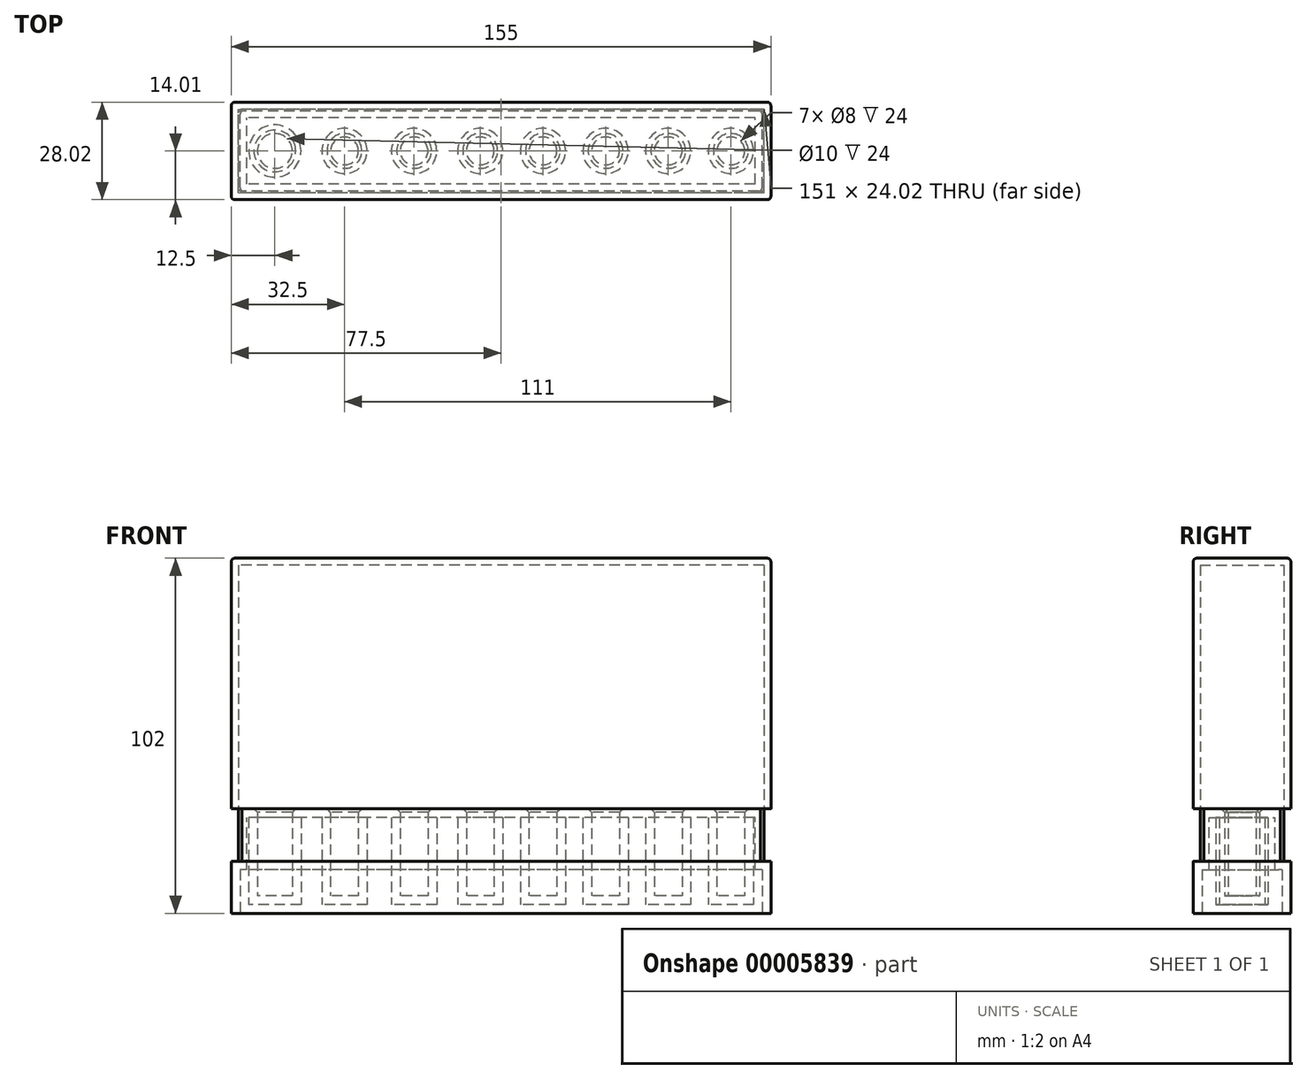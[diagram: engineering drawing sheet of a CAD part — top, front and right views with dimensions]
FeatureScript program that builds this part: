
annotation { "Feature Type Name" : "Feature", "Feature Type Description" : "" }
export const myFeature = defineFeature(function(context is Context, id is Id, definition is map)
    precondition{}
    {
        {
            var Q0;
            Q0=qCreatedBy(makeId("Top.planeOp"),FACE);
            var sketch = newSketch(context, id + "F0", { "sketchPlane" : qUnion([Q0])});
            skCircle(sketch, "E0", {"center": v(-65.5, 0) * mm, "radius": 7.5 * mm, "construction": true});
            skCircle(sketch, "E1.1.0.0", {"center": v(-45.5, 0) * mm, "radius": 7.5 * mm, "construction": true});
            skCircle(sketch, "E1.2.0.0", {"center": v(-25.5, 0) * mm, "radius": 7.5 * mm, "construction": true});
            skCircle(sketch, "E1.3.0.0", {"center": v(-6.5, 0) * mm, "radius": 6.5 * mm, "construction": true});
            skCircle(sketch, "E1.4.0.0", {"center": v(11.5, 0) * mm, "radius": 6.5 * mm, "construction": true});
            skCircle(sketch, "E1.5.0.0", {"center": v(29.5, 0) * mm, "radius": 6.5 * mm, "construction": true});
            skCircle(sketch, "E1.6.0.0", {"center": v(47.5, 0) * mm, "radius": 6.5 * mm, "construction": true});
            skCircle(sketch, "E1.7.0.0", {"center": v(65.5, 0) * mm, "radius": 6.5 * mm, "construction": true});
            skCircle(sketch, "E2", {"center": v(-65.5, 0) * mm, "radius": 5 * mm});
            skCircle(sketch, "E3", {"center": v(-45.5, 0) * mm, "radius": 4 * mm});
            skCircle(sketch, "E4", {"center": v(-25.5, 0) * mm, "radius": 4 * mm});
            skCircle(sketch, "E5", {"center": v(-6.5, 0) * mm, "radius": 4 * mm});
            skCircle(sketch, "E6", {"center": v(11.5, 0) * mm, "radius": 4 * mm});
            skCircle(sketch, "E7", {"center": v(29.5, 0) * mm, "radius": 4 * mm});
            skCircle(sketch, "E8", {"center": v(47.5, 0) * mm, "radius": 4 * mm});
            skCircle(sketch, "E9", {"center": v(65.5, 0) * mm, "radius": 4 * mm});
            skPoint(sketch, "E10", {"position": v(0, 0) * mm});
            skLineSegment(sketch, "E11.bottom", {"start": v(77, -14) * mm, "end": v(-78, -14) * mm});
            skLineSegment(sketch, "E11.top", {"start": v(77, 14) * mm, "end": v(-78, 14) * mm});
            skLineSegment(sketch, "E11.left", {"start": v(77, -14) * mm, "end": v(77, 14) * mm});
            skLineSegment(sketch, "E11.right", {"start": v(-78, -14) * mm, "end": v(-78, 14) * mm});
            skLineSegment(sketch, "E12", {"start": v(-82.74, 0) * mm, "end": v(89.14, 0) * mm, "construction": true});
            skLineSegment(sketch, "E13.0", {"start": v(-76, -12) * mm, "end": v(-76, 12) * mm});
            skLineSegment(sketch, "E13.1", {"start": v(75, -12) * mm, "end": v(-76, -12) * mm});
            skLineSegment(sketch, "E13.2", {"start": v(75, -12) * mm, "end": v(75, 12) * mm});
            skLineSegment(sketch, "E13.3", {"start": v(75, 12) * mm, "end": v(-76, 12) * mm});
            skSolve(sketch);
        }
        {
            var Q0;
            Q0=makeQuery(id+"F0.imprint","IMPRINT",FACE,{"disambiguationData":[TD([[makeQuery(id+"F0.imprint","IMPRINT",EDGE,{"derivedFrom":sQuery(id+"F0.wireOp",EDGE,"E2")}),-1.0]])]});
            var Q1;
            Q1=makeQuery(id+"F0.imprint","IMPRINT",FACE,{"disambiguationData":[TD([[makeQuery(id+"F0.imprint","IMPRINT",EDGE,{"derivedFrom":sQuery(id+"F0.wireOp",EDGE,"E11.bottom")}),-1.0]])]});
            extrude(context, id + "F1", {"entities" : qUnion([Q0, Q1]), "depth" : 25 * mm, "offsetDistance" : 25 * mm});
        }
        {
            var Q0;
            Q0=makeQuery(id+"F0.imprint","IMPRINT",FACE,{"disambiguationData":[TD([[makeQuery(id+"F0.imprint","IMPRINT",EDGE,{"derivedFrom":sQuery(id+"F0.wireOp",EDGE,"E6")}),1.0]])]});
            var Q1;
            Q1=makeQuery(id+"F0.imprint","IMPRINT",FACE,{"disambiguationData":[TD([[makeQuery(id+"F0.imprint","IMPRINT",EDGE,{"derivedFrom":sQuery(id+"F0.wireOp",EDGE,"E3")}),1.0]])]});
            var Q2;
            Q2=makeQuery(id+"F0.imprint","IMPRINT",FACE,{"disambiguationData":[TD([[makeQuery(id+"F0.imprint","IMPRINT",EDGE,{"derivedFrom":sQuery(id+"F0.wireOp",EDGE,"E2")}),1.0]])]});
            var Q3;
            Q3=makeQuery(id+"F0.imprint","IMPRINT",FACE,{"disambiguationData":[TD([[makeQuery(id+"F0.imprint","IMPRINT",EDGE,{"derivedFrom":sQuery(id+"F0.wireOp",EDGE,"E4")}),1.0]])]});
            var Q4;
            Q4=makeQuery(id+"F0.imprint","IMPRINT",FACE,{"disambiguationData":[TD([[makeQuery(id+"F0.imprint","IMPRINT",EDGE,{"derivedFrom":sQuery(id+"F0.wireOp",EDGE,"E5")}),1.0]])]});
            var Q5;
            Q5=makeQuery(id+"F0.imprint","IMPRINT",FACE,{"disambiguationData":[TD([[makeQuery(id+"F0.imprint","IMPRINT",EDGE,{"derivedFrom":sQuery(id+"F0.wireOp",EDGE,"E7")}),1.0]])]});
            var Q6;
            Q6=makeQuery(id+"F0.imprint","IMPRINT",FACE,{"disambiguationData":[TD([[makeQuery(id+"F0.imprint","IMPRINT",EDGE,{"derivedFrom":sQuery(id+"F0.wireOp",EDGE,"E8")}),1.0]])]});
            var Q7;
            Q7=makeQuery(id+"F0.imprint","IMPRINT",FACE,{"disambiguationData":[TD([[makeQuery(id+"F0.imprint","IMPRINT",EDGE,{"derivedFrom":sQuery(id+"F0.wireOp",EDGE,"E2")}),-1.0]])]});
            var Q8;
            Q8=makeQuery(id+"F0.imprint","IMPRINT",FACE,{"disambiguationData":[TD([[makeQuery(id+"F0.imprint","IMPRINT",EDGE,{"derivedFrom":sQuery(id+"F0.wireOp",EDGE,"E9")}),1.0]])]});
            var Q9;
            Q9=makeQuery(id+"F0.imprint","IMPRINT",FACE,{"disambiguationData":[TD([[makeQuery(id+"F0.imprint","IMPRINT",EDGE,{"derivedFrom":sQuery(id+"F0.wireOp",EDGE,"E11.bottom")}),-1.0]])]});
            extrude(context, id + "F2", {"entities" : qUnion([Q0, Q1, Q2, Q3, Q4, Q5, Q6, Q7, Q8, Q9]), "operationType" : NewBodyOperationType.ADD, "oppositeDirection" : true, "depth" : 5 * mm, "offsetDistance" : 25 * mm});
        }
        {
            var Q0;
            Q0=makeQuery(id+"F1.opExtrude","CAP_FACE",FACE,{"disambiguationData":[OSD([sQuery(id+"F0.wireOp",EDGE,"E2"),sQuery(id+"F0.wireOp",EDGE,"E3"),sQuery(id+"F0.wireOp",EDGE,"E4"),sQuery(id+"F0.wireOp",EDGE,"E5"),sQuery(id+"F0.wireOp",EDGE,"E6"),sQuery(id+"F0.wireOp",EDGE,"E7"),sQuery(id+"F0.wireOp",EDGE,"E8"),sQuery(id+"F0.wireOp",EDGE,"E9"),sQuery(id+"F0.wireOp",EDGE,"E11.bottom"),sQuery(id+"F0.wireOp",EDGE,"E11.top"),sQuery(id+"F0.wireOp",EDGE,"E11.left"),sQuery(id+"F0.wireOp",EDGE,"E11.right")])],"isStart":false});
            var sketch = newSketch(context, id + "F3", { "sketchPlane" : qUnion([Q0])});
            skLineSegment(sketch, "E14.0", {"start": v(75, -12) * mm, "end": v(-76, -12) * mm});
            skLineSegment(sketch, "E15.0", {"start": v(-76, -12) * mm, "end": v(-76, 12) * mm});
            skLineSegment(sketch, "E16.0", {"start": v(75, 12) * mm, "end": v(-76, 12) * mm});
            skLineSegment(sketch, "E17.0", {"start": v(77, -14) * mm, "end": v(77, 14) * mm});
            skLineSegment(sketch, "E18.0", {"start": v(75, -12) * mm, "end": v(75, 12) * mm});
            skSolve(sketch);
        }
        {
            var Q0;
            Q0=makeQuery(id+"F3.imprint","IMPRINT",FACE,{"disambiguationData":[TD([[makeQuery(id+"F3.imprint","IMPRINT",EDGE,{"derivedFrom":sQuery(id+"F3.wireOp",EDGE,"E14.0")}),1.0]])]});
            var Q1;
            Q1=makeQuery(id+"F3.imprint","IMPRINT",FACE,{"disambiguationData":[TD([[makeQuery(id+"F3.imprint","IMPRINT",EDGE,{"derivedFrom":sQuery(id+"F3.wireOp",EDGE,"E14.0")}),-1.0]])]});
            var Q2;
            Q2=makeQuery(id+"F3.imprint","IMPRINT",FACE,{"disambiguationData":[TD([[makeQuery(id+"F3.imprint","IMPRINT",EDGE,{"derivedFrom":makeQuery(id+"F1.opExtrude","CAP_EDGE",EDGE,{"disambiguationData":[OSD([sQuery(id+"F0.wireOp",EDGE,"E2")])],"isStart":false})}),1.0]])]});
            var Q3;
            Q3=makeQuery(id+"F3.imprint","IMPRINT",FACE,{"disambiguationData":[TD([[makeQuery(id+"F3.imprint","IMPRINT",EDGE,{"derivedFrom":makeQuery(id+"F1.opExtrude","CAP_EDGE",EDGE,{"disambiguationData":[OSD([sQuery(id+"F0.wireOp",EDGE,"E3")])],"isStart":false})}),1.0]])]});
            var Q4;
            Q4=makeQuery(id+"F3.imprint","IMPRINT",FACE,{"disambiguationData":[TD([[makeQuery(id+"F3.imprint","IMPRINT",EDGE,{"derivedFrom":makeQuery(id+"F1.opExtrude","CAP_EDGE",EDGE,{"disambiguationData":[OSD([sQuery(id+"F0.wireOp",EDGE,"E4")])],"isStart":false})}),1.0]])]});
            var Q5;
            Q5=makeQuery(id+"F3.imprint","IMPRINT",FACE,{"disambiguationData":[TD([[makeQuery(id+"F3.imprint","IMPRINT",EDGE,{"derivedFrom":makeQuery(id+"F1.opExtrude","CAP_EDGE",EDGE,{"disambiguationData":[OSD([sQuery(id+"F0.wireOp",EDGE,"E5")])],"isStart":false})}),1.0]])]});
            var Q6;
            Q6=makeQuery(id+"F3.imprint","IMPRINT",FACE,{"disambiguationData":[TD([[makeQuery(id+"F3.imprint","IMPRINT",EDGE,{"derivedFrom":makeQuery(id+"F1.opExtrude","CAP_EDGE",EDGE,{"disambiguationData":[OSD([sQuery(id+"F0.wireOp",EDGE,"E6")])],"isStart":false})}),1.0]])]});
            var Q7;
            Q7=makeQuery(id+"F3.imprint","IMPRINT",FACE,{"disambiguationData":[TD([[makeQuery(id+"F3.imprint","IMPRINT",EDGE,{"derivedFrom":makeQuery(id+"F1.opExtrude","CAP_EDGE",EDGE,{"disambiguationData":[OSD([sQuery(id+"F0.wireOp",EDGE,"E7")])],"isStart":false})}),1.0]])]});
            var Q8;
            Q8=makeQuery(id+"F3.imprint","IMPRINT",FACE,{"disambiguationData":[TD([[makeQuery(id+"F3.imprint","IMPRINT",EDGE,{"derivedFrom":makeQuery(id+"F1.opExtrude","CAP_EDGE",EDGE,{"disambiguationData":[OSD([sQuery(id+"F0.wireOp",EDGE,"E8")])],"isStart":false})}),1.0]])]});
            var Q9;
            Q9=makeQuery(id+"F3.imprint","IMPRINT",FACE,{"disambiguationData":[TD([[makeQuery(id+"F3.imprint","IMPRINT",EDGE,{"derivedFrom":makeQuery(id+"F1.opExtrude","CAP_EDGE",EDGE,{"disambiguationData":[OSD([sQuery(id+"F0.wireOp",EDGE,"E9")])],"isStart":false})}),1.0]])]});
            extrude(context, id + "F4", {"entities" : qUnion([Q0, Q1, Q2, Q3, Q4, Q5, Q6, Q7, Q8, Q9]), "depth" : 72 * mm, "offsetDistance" : 25 * mm, "hasSecondDirection" : true, "secondDirectionOppositeDirection" : true, "secondDirectionDepth" : 15 * mm});
        }
        {
            var Q0;
            Q0=makeQuery(id+"F4.opExtrude","CAP_FACE",FACE,{"disambiguationData":[OSD([sQuery(id+"F0.wireOp",EDGE,"E11.bottom"),sQuery(id+"F0.wireOp",EDGE,"E11.top"),sQuery(id+"F0.wireOp",EDGE,"E11.right"),sQuery(id+"F3.wireOp",EDGE,"E17.0")])],"isStart":true});
            shell(context, id + "F5", {"entities" : qUnion([Q0]), "thickness" : 2 * mm});
        }
        {
            var Q0;
            Q0=makeQuery(id+"F3.imprint","IMPRINT",FACE,{"disambiguationData":[TD([[makeQuery(id+"F3.imprint","IMPRINT",EDGE,{"derivedFrom":sQuery(id+"F3.wireOp",EDGE,"E14.0")}),1.0]])]});
            extrude(context, id + "F6", {"entities" : qUnion([Q0]), "operationType" : NewBodyOperationType.REMOVE, "oppositeDirection" : true, "depth" : 15 * mm, "offsetDistance" : 25 * mm});
        }
        {
            var Q0;
            Q0=makeQuery(id+"F2.opExtrude","CAP_FACE",FACE,{"disambiguationData":[OSD([sQuery(id+"F0.wireOp",EDGE,"E11.bottom"),sQuery(id+"F0.wireOp",EDGE,"E11.top"),sQuery(id+"F0.wireOp",EDGE,"E11.left"),sQuery(id+"F0.wireOp",EDGE,"E11.right")])],"isStart":false});
            shell(context, id + "F7", {"entities" : qUnion([Q0]), "thickness" : 2.5 * mm});
        }
        {
            var Q0;
            Q0=makeQuery(id+"F6.boolean.opBoolean","COPY",EDGE,{"derivedFrom":makeQuery(id+"F6.opExtrude","CAP_EDGE",EDGE,{"disambiguationData":[OSD([sQuery(id+"F3.wireOp",EDGE,"E16.0")])],"isStart":true})});
            var Q1;
            Q1=makeQuery(id+"F6.boolean.opBoolean","COPY",EDGE,{"derivedFrom":makeQuery(id+"F6.opExtrude","CAP_EDGE",EDGE,{"disambiguationData":[OSD([sQuery(id+"F3.wireOp",EDGE,"E18.0")])],"isStart":true})});
            var Q2;
            Q2=makeQuery(id+"F6.boolean.opBoolean","COPY",EDGE,{"derivedFrom":makeQuery(id+"F6.opExtrude","CAP_EDGE",EDGE,{"disambiguationData":[OSD([sQuery(id+"F3.wireOp",EDGE,"E14.0")])],"isStart":true})});
            var Q3;
            Q3=makeQuery(id+"F6.boolean.opBoolean","COPY",EDGE,{"derivedFrom":makeQuery(id+"F6.opExtrude","CAP_EDGE",EDGE,{"disambiguationData":[OSD([sQuery(id+"F3.wireOp",EDGE,"E15.0")])],"isStart":true})});
            var Q4;
            Q4=makeQuery(id+"F6.boolean.opBoolean","COPY",EDGE,{"derivedFrom":makeQuery(id+"F6.opExtrude","SWEPT_EDGE",EDGE,{"disambiguationData":[OSD([sQuery(id+"F3.wireOp",EDGE,"E15.0"),sQuery(id+"F3.wireOp",EDGE,"E16.0")])]})});
            var Q5;
            Q5=makeQuery(id+"F6.boolean.opBoolean","COPY",EDGE,{"derivedFrom":makeQuery(id+"F6.opExtrude","SWEPT_EDGE",EDGE,{"disambiguationData":[OSD([sQuery(id+"F3.wireOp",EDGE,"E16.0"),sQuery(id+"F3.wireOp",EDGE,"E18.0")])]})});
            var Q6;
            Q6=makeQuery(id+"F6.boolean.opBoolean","COPY",EDGE,{"derivedFrom":makeQuery(id+"F6.opExtrude","SWEPT_EDGE",EDGE,{"disambiguationData":[OSD([sQuery(id+"F3.wireOp",EDGE,"E14.0"),sQuery(id+"F3.wireOp",EDGE,"E18.0")])]})});
            var Q7;
            Q7=makeQuery(id+"F6.boolean.opBoolean","COPY",EDGE,{"derivedFrom":makeQuery(id+"F6.opExtrude","SWEPT_EDGE",EDGE,{"disambiguationData":[OSD([sQuery(id+"F3.wireOp",EDGE,"E14.0"),sQuery(id+"F3.wireOp",EDGE,"E15.0")])]})});
            var Q8;
            Q8=makeQuery(id+"F1.opExtrude","CAP_EDGE",EDGE,{"disambiguationData":[OSD([sQuery(id+"F0.wireOp",EDGE,"E2")])],"isStart":false});
            var Q9;
            Q9=makeQuery(id+"F1.opExtrude","CAP_EDGE",EDGE,{"disambiguationData":[OSD([sQuery(id+"F0.wireOp",EDGE,"E3")])],"isStart":false});
            var Q10;
            Q10=makeQuery(id+"F1.opExtrude","CAP_EDGE",EDGE,{"disambiguationData":[OSD([sQuery(id+"F0.wireOp",EDGE,"E4")])],"isStart":false});
            var Q11;
            Q11=makeQuery(id+"F1.opExtrude","CAP_EDGE",EDGE,{"disambiguationData":[OSD([sQuery(id+"F0.wireOp",EDGE,"E5")])],"isStart":false});
            var Q12;
            Q12=makeQuery(id+"F1.opExtrude","CAP_EDGE",EDGE,{"disambiguationData":[OSD([sQuery(id+"F0.wireOp",EDGE,"E6")])],"isStart":false});
            var Q13;
            Q13=makeQuery(id+"F1.opExtrude","CAP_EDGE",EDGE,{"disambiguationData":[OSD([sQuery(id+"F0.wireOp",EDGE,"E7")])],"isStart":false});
            var Q14;
            Q14=makeQuery(id+"F1.opExtrude","CAP_EDGE",EDGE,{"disambiguationData":[OSD([sQuery(id+"F0.wireOp",EDGE,"E8")])],"isStart":false});
            var Q15;
            Q15=makeQuery(id+"F1.opExtrude","CAP_EDGE",EDGE,{"disambiguationData":[OSD([sQuery(id+"F0.wireOp",EDGE,"E9")])],"isStart":false});
            chamfer(context, id + "F8", {"entities" : qUnion([Q0, Q1, Q2, Q3, Q4, Q5, Q6, Q7, Q8, Q9, Q10, Q11, Q12, Q13, Q14, Q15]), "width" : 1 * mm, "tangentPropagation" : true});
        }
        {
            var Q0;
            Q0=makeQuery(id+"F4.opExtrude","SWEPT_EDGE",EDGE,{"disambiguationData":[OSD([sQuery(id+"F0.wireOp",EDGE,"E11.bottom"),sQuery(id+"F3.wireOp",EDGE,"E17.0")])]});
            var Q1;
            Q1=makeQuery(id+"F4.opExtrude","SWEPT_EDGE",EDGE,{"disambiguationData":[OSD([sQuery(id+"F0.wireOp",EDGE,"E11.top"),sQuery(id+"F3.wireOp",EDGE,"E17.0")])]});
            var Q2;
            Q2=makeQuery(id+"F4.opExtrude","SWEPT_EDGE",EDGE,{"disambiguationData":[OSD([sQuery(id+"F0.wireOp",EDGE,"E11.top"),sQuery(id+"F0.wireOp",EDGE,"E11.right")])]});
            var Q3;
            Q3=makeQuery(id+"F4.opExtrude","SWEPT_EDGE",EDGE,{"disambiguationData":[OSD([sQuery(id+"F0.wireOp",EDGE,"E11.bottom"),sQuery(id+"F0.wireOp",EDGE,"E11.right")])]});
            var Q4;
            Q4=makeQuery(id+"F4.opExtrude","CAP_EDGE",EDGE,{"disambiguationData":[OSD([sQuery(id+"F0.wireOp",EDGE,"E11.right")])],"isStart":false});
            var Q5;
            Q5=makeQuery(id+"F4.opExtrude","CAP_EDGE",EDGE,{"disambiguationData":[OSD([sQuery(id+"F0.wireOp",EDGE,"E11.top")])],"isStart":false});
            var Q6;
            Q6=makeQuery(id+"F4.opExtrude","CAP_EDGE",EDGE,{"disambiguationData":[OSD([sQuery(id+"F3.wireOp",EDGE,"E17.0")])],"isStart":false});
            var Q7;
            Q7=makeQuery(id+"F4.opExtrude","CAP_EDGE",EDGE,{"disambiguationData":[OSD([sQuery(id+"F0.wireOp",EDGE,"E11.bottom")])],"isStart":false});
            var Q8;
            {var subQ0=sQuery(id+"F0.wireOp",EDGE,"E11.right");var subQ1=sQuery(id+"F0.wireOp",EDGE,"E11.top");Q8=makeQuery(id+"F2.boolean.opBoolean","MERGE",EDGE,{"derivedFrom":[makeQuery(id+"F1.opExtrude","SWEPT_EDGE",EDGE,{"disambiguationData":[OSD([subQ1,subQ0])]}),makeQuery(id+"F2.opExtrude","SWEPT_EDGE",EDGE,{"disambiguationData":[OSD([subQ1,subQ0])]})]});}
            var Q9;
            {var subQ0=sQuery(id+"F0.wireOp",EDGE,"E11.right");var subQ1=sQuery(id+"F0.wireOp",EDGE,"E11.bottom");Q9=makeQuery(id+"F2.boolean.opBoolean","MERGE",EDGE,{"derivedFrom":[makeQuery(id+"F1.opExtrude","SWEPT_EDGE",EDGE,{"disambiguationData":[OSD([subQ1,subQ0])]}),makeQuery(id+"F2.opExtrude","SWEPT_EDGE",EDGE,{"disambiguationData":[OSD([subQ1,subQ0])]})]});}
            var Q10;
            {var subQ0=sQuery(id+"F0.wireOp",EDGE,"E11.left");var subQ1=sQuery(id+"F0.wireOp",EDGE,"E11.bottom");Q10=makeQuery(id+"F2.boolean.opBoolean","MERGE",EDGE,{"derivedFrom":[makeQuery(id+"F1.opExtrude","SWEPT_EDGE",EDGE,{"disambiguationData":[OSD([subQ1,subQ0])]}),makeQuery(id+"F2.opExtrude","SWEPT_EDGE",EDGE,{"disambiguationData":[OSD([subQ1,subQ0])]})]});}
            var Q11;
            {var subQ0=sQuery(id+"F0.wireOp",EDGE,"E11.left");var subQ1=sQuery(id+"F0.wireOp",EDGE,"E11.top");Q11=makeQuery(id+"F2.boolean.opBoolean","MERGE",EDGE,{"derivedFrom":[makeQuery(id+"F1.opExtrude","SWEPT_EDGE",EDGE,{"disambiguationData":[OSD([subQ1,subQ0])]}),makeQuery(id+"F2.opExtrude","SWEPT_EDGE",EDGE,{"disambiguationData":[OSD([subQ1,subQ0])]})]});}
            var Q12;
            Q12=makeQuery(id+"F7.opShell","OFFSET_EDGE",EDGE,{"disambiguationData":[OSD([sQuery(id+"F0.wireOp",EDGE,"E11.bottom"),sQuery(id+"F0.wireOp",EDGE,"E11.left")])]});
            var Q13;
            Q13=makeQuery(id+"F7.opShell","OFFSET_EDGE",EDGE,{"disambiguationData":[OSD([sQuery(id+"F0.wireOp",EDGE,"E11.top"),sQuery(id+"F0.wireOp",EDGE,"E11.left")])]});
            var Q14;
            Q14=makeQuery(id+"F7.opShell","OFFSET_EDGE",EDGE,{"disambiguationData":[OSD([sQuery(id+"F0.wireOp",EDGE,"E11.bottom"),sQuery(id+"F0.wireOp",EDGE,"E11.right")])]});
            var Q15;
            Q15=makeQuery(id+"F7.opShell","OFFSET_EDGE",EDGE,{"disambiguationData":[OSD([sQuery(id+"F0.wireOp",EDGE,"E11.top"),sQuery(id+"F0.wireOp",EDGE,"E11.right")])]});
            fillet(context, id + "F9", {"entities" : qUnion([Q0, Q1, Q2, Q3, Q4, Q5, Q6, Q7, Q8, Q9, Q10, Q11, Q12, Q13, Q14, Q15]), "radius" : 1 * mm, "tangentPropagation" : true, "allowEdgeOverflow" : false});
        }
    });
